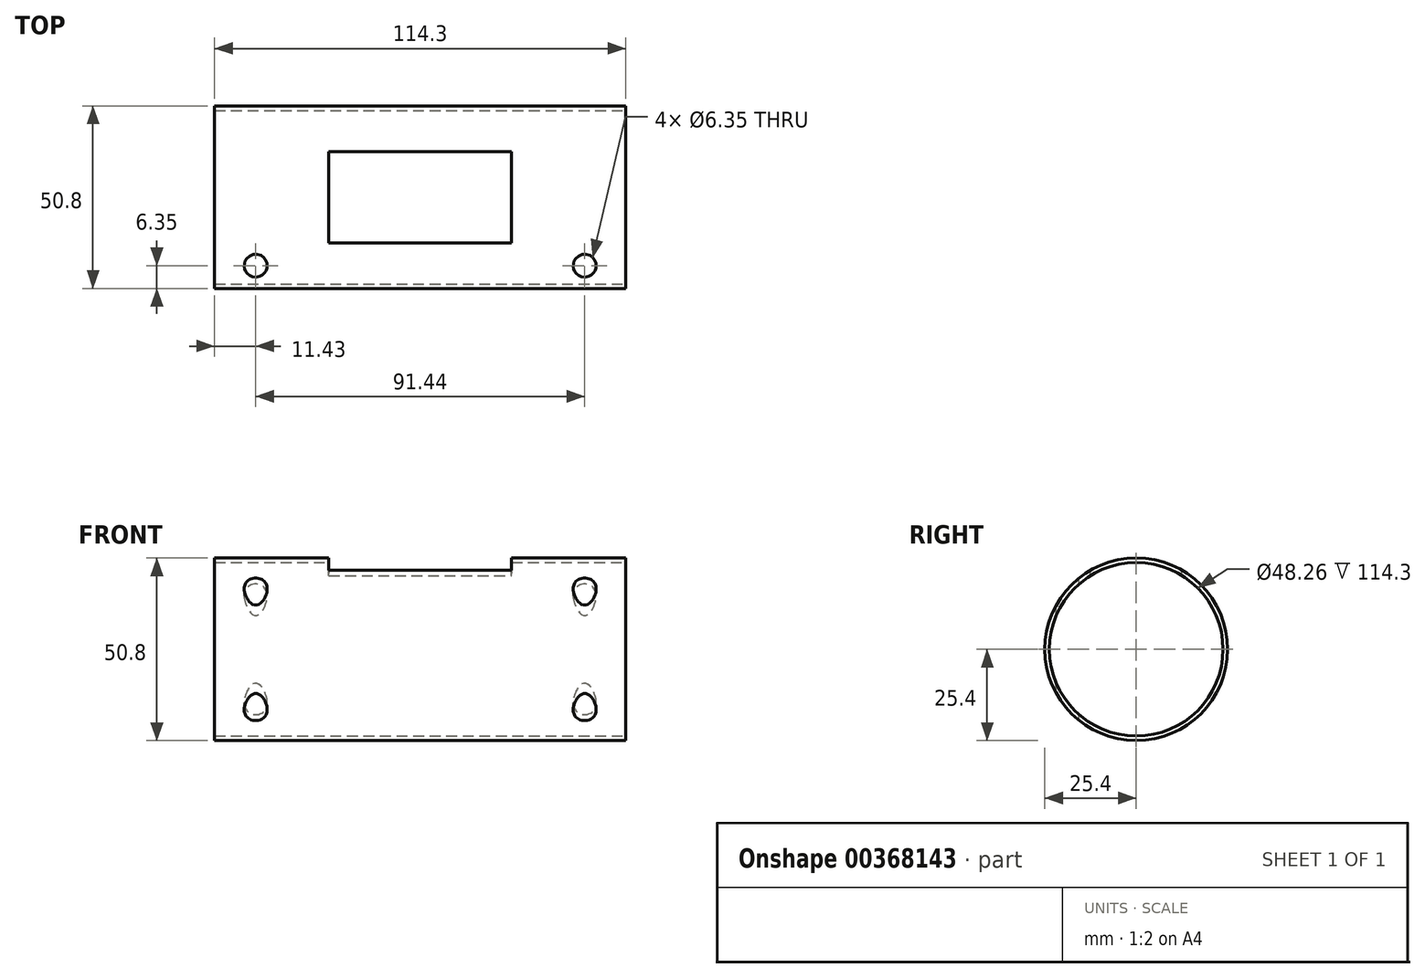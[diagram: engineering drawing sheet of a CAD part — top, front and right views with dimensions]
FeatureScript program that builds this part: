
annotation { "Feature Type Name" : "Feature", "Feature Type Description" : "" }
export const myFeature = defineFeature(function(context is Context, id is Id, definition is map)
    precondition{}
    {
        {
            var Q0;
            Q0=qCreatedBy(makeId("Right.planeOp"),FACE);
            var sketch = newSketch(context, id + "F0", { "sketchPlane" : qUnion([Q0])});
            skPoint(sketch, "E0.first.point", {"position": v(0, 0) * mm});
            skCircle(sketch, "E1", {"center": v(0, -25.4) * mm, "radius": 25.4 * mm});
            skSolve(sketch);
        }
        {
            var Q0;
            Q0=makeQuery(id+"F0.imprint","IMPRINT",FACE,{"disambiguationData":[TD([[makeQuery(id+"F0.imprint","IMPRINT",EDGE,{"derivedFrom":sQuery(id+"F0.wireOp",EDGE,"E1")}),1.0]])]});
            extrude(context, id + "F1", {"entities" : qUnion([Q0]), "depth" : 114.3 * mm, "symmetric" : true});
        }
        {
            var Q0;
            Q0=qCreatedBy(makeId("Top.planeOp"),FACE);
            var sketch = newSketch(context, id + "F2", { "sketchPlane" : qUnion([Q0])});
            skLineSegment(sketch, "E2", {"start": v(-25.4, 0) * mm, "end": v(-25.4, 12.7) * mm});
            skLineSegment(sketch, "E3", {"start": v(25.4, 0) * mm, "end": v(25.4, -12.7) * mm});
            skLineSegment(sketch, "E4.bottom", {"start": v(-25.4, 12.7) * mm, "end": v(25.4, 12.7) * mm});
            skLineSegment(sketch, "E4.top", {"start": v(-25.4, -12.7) * mm, "end": v(25.4, -12.7) * mm});
            skLineSegment(sketch, "E4.left", {"start": v(-25.4, 12.7) * mm, "end": v(-25.4, -12.7) * mm});
            skLineSegment(sketch, "E4.right", {"start": v(25.4, 12.7) * mm, "end": v(25.4, -12.7) * mm});
            skSolve(sketch);
        }
        {
            var Q0;
            {var subQ0=sQuery(id+"F2.wireOp",EDGE,"E4.bottom");Q0=makeQuery(id+"F2.imprint","IMPRINT",FACE,{"disambiguationData":[TD([[makeQuery(id+"F2.imprint","IMPRINT",EDGE,{"derivedFrom":subQ0}),-1.0]])]});}
            extrude(context, id + "F3", {"entities" : qUnion([Q0]), "operationType" : NewBodyOperationType.REMOVE, "oppositeDirection" : true, "depth" : 25.4 * mm});
        }
        {
            var Q0;
            Q0=makeQuery(id+"F1.opExtrude","CAP_FACE",FACE,{"disambiguationData":[OSD([sQuery(id+"F0.wireOp",EDGE,"E1")])],"isStart":false});
            var sketch = newSketch(context, id + "F4", { "sketchPlane" : qUnion([Q0])});
            skLineSegment(sketch, "E5", {"start": v(0, 0) * mm, "end": v(0, -25.4) * mm});
            skCircle(sketch, "E6", {"center": v(0, -25.4) * mm, "radius": 24.13 * mm});
            skSolve(sketch);
        }
        {
            var Q0;
            Q0=makeQuery(id+"F4.imprint","IMPRINT",FACE,{"disambiguationData":[TD([[makeQuery(id+"F4.imprint","IMPRINT",EDGE,{"derivedFrom":sQuery(id+"F4.wireOp",EDGE,"E6")}),1.0]])]});
            extrude(context, id + "F5", {"entities" : qUnion([Q0]), "operationType" : NewBodyOperationType.REMOVE, "oppositeDirection" : true, "depth" : 114.3 * mm});
        }
        {
            var Q0;
            Q0=qCreatedBy(makeId("Top.planeOp"),FACE);
            var sketch = newSketch(context, id + "F6", { "sketchPlane" : qUnion([Q0])});
            skLineSegment(sketch, "E7", {"start": v(0, 0) * mm, "end": v(-45.72, 0) * mm});
            skLineSegment(sketch, "E8", {"start": v(-45.72, 0) * mm, "end": v(-45.72, -19.05) * mm});
            skLineSegment(sketch, "E9", {"start": v(0, 0) * mm, "end": v(45.72, 0) * mm});
            skLineSegment(sketch, "E10", {"start": v(45.72, 0) * mm, "end": v(45.72, -19.05) * mm});
            skCircle(sketch, "E11", {"center": v(-45.72, -19.05) * mm, "radius": 3.18 * mm});
            skCircle(sketch, "E12", {"center": v(45.72, -19.05) * mm, "radius": 3.18 * mm});
            skSolve(sketch);
        }
        {
            var Q0;
            Q0=makeQuery(id+"F6.imprint","IMPRINT",FACE,{"disambiguationData":[TD([[makeQuery(id+"F6.imprint","IMPRINT",EDGE,{"derivedFrom":sQuery(id+"F6.wireOp",EDGE,"E11")}),1.0]])]});
            var Q1;
            Q1=makeQuery(id+"F6.imprint","IMPRINT",FACE,{"disambiguationData":[TD([[makeQuery(id+"F6.imprint","IMPRINT",EDGE,{"derivedFrom":sQuery(id+"F6.wireOp",EDGE,"E12")}),1.0]])]});
            extrude(context, id + "F7", {"entities" : qUnion([Q0, Q1]), "operationType" : NewBodyOperationType.REMOVE, "oppositeDirection" : true, "depth" : 76.2 * mm});
        }
    });
